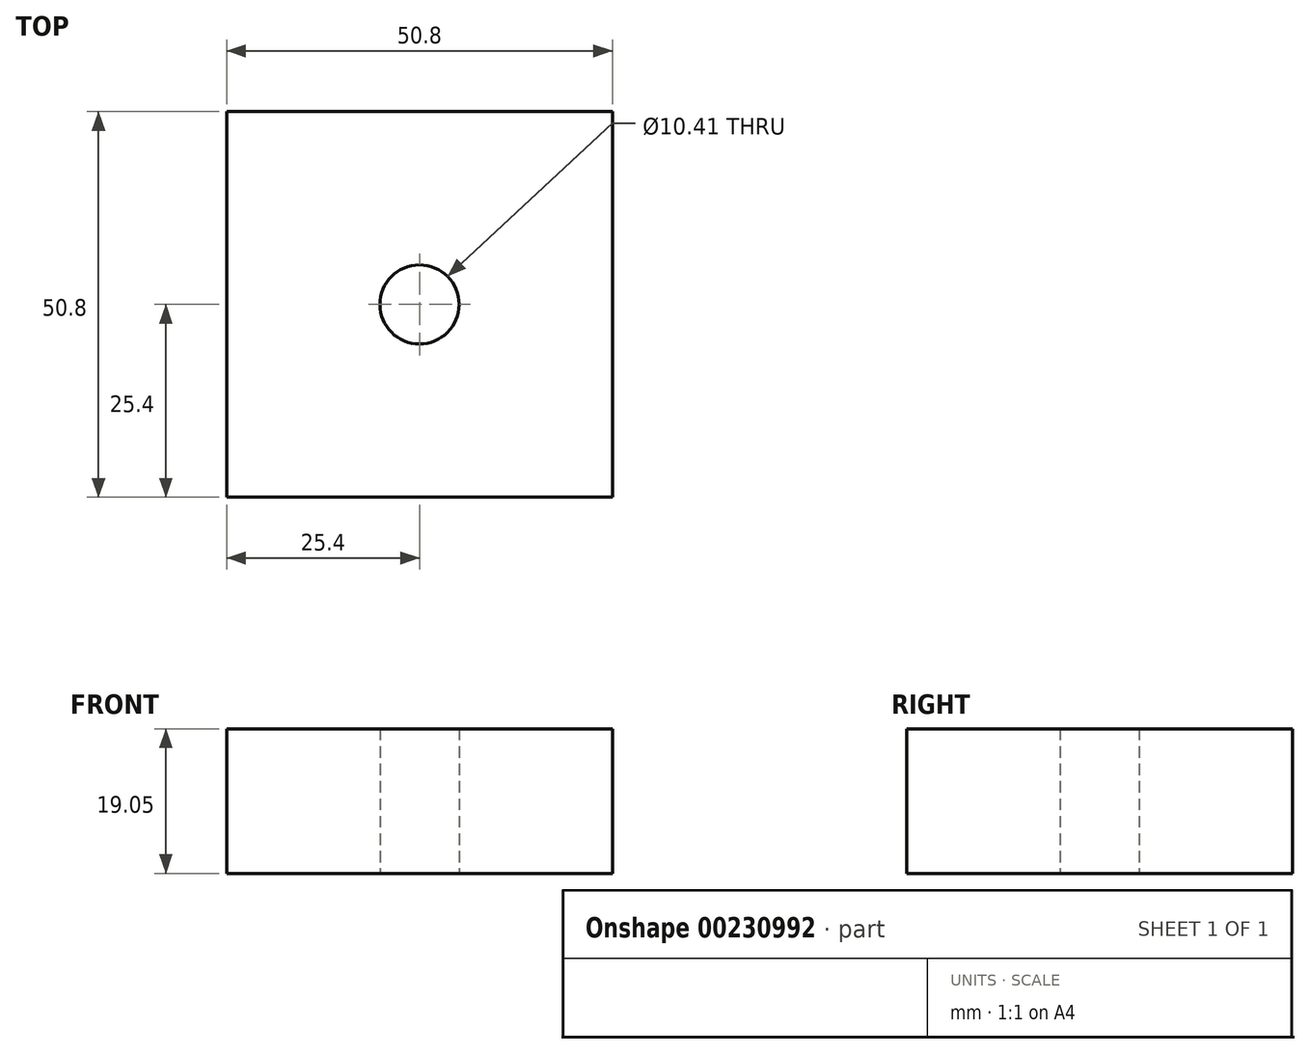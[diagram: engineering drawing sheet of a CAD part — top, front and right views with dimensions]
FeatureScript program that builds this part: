
annotation { "Feature Type Name" : "Feature", "Feature Type Description" : "" }
export const myFeature = defineFeature(function(context is Context, id is Id, definition is map)
    precondition{}
    {
        {
            var Q0;
            Q0=qCreatedBy(makeId("Top.planeOp"),FACE);
            var sketch = newSketch(context, id + "F0", { "sketchPlane" : qUnion([Q0])});
            skLineSegment(sketch, "E0.bottom", {"start": v(25.4, -25.4) * mm, "end": v(-25.4, -25.4) * mm});
            skLineSegment(sketch, "E0.top", {"start": v(25.4, 25.4) * mm, "end": v(-25.4, 25.4) * mm});
            skLineSegment(sketch, "E0.left", {"start": v(25.4, -25.4) * mm, "end": v(25.4, 25.4) * mm});
            skLineSegment(sketch, "E0.right", {"start": v(-25.4, -25.4) * mm, "end": v(-25.4, 25.4) * mm});
            skPoint(sketch, "E0.middle", {"position": v(0, 0) * mm});
            skCircle(sketch, "E1", {"center": v(0, 0) * mm, "radius": 5.2 * mm});
            skSolve(sketch);
        }
        {
            var Q0;
            Q0 = qSketchRegion(id + "F0", true);
            extrude(context, id + "F1", {"entities" : qUnion([Q0]), "depth" : 19.05 * mm, "offsetDistance" : 25 * mm});
        }
    });
